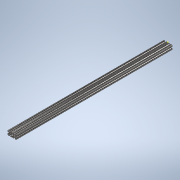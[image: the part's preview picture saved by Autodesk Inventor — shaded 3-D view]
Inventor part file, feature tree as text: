
AUTODESK INVENTOR PART (.ipt)
format: ipt  version: 2020 (Build 240168000, 168)  size: 362,496 bytes
history: native  units: in
note: dims shown in document units (in); Inventor stores cm internally (conversion verified against a paired STEP export)
features: sketch x2, extrude x1
ambient origin geometry x8: Origin, YZ Plane, XZ Plane, XY Plane, X Axis, Y Axis, Z Axis, Center Point
bodies: Solid1 (feature_tree)
feature tree (3):
  extrude  "Extrusion1"  [1 undecoded]
  sketch  "Sketch2"
  sketch  "Sketch1"  dims[d0=36.0in d1=0.0in]
note: 1 required parameter value undecoded (feature->parameter linkage not recoverable at this tier; creation-order binding heuristic only, values carry confidence <= 0.55)
